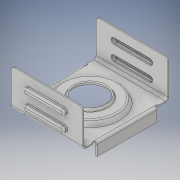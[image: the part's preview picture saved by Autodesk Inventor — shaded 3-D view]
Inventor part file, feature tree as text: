
AUTODESK INVENTOR PART (.ipt)
format: ipt  version: 2019 (Build 230136000, 136)  size: 508,928 bytes
history: native  units: mm
features: sketch x9, sheet_metal_op x5, plane x4, fillet x3, chamfer x2, shell x2, revolve x1, extrude x1, mirror x1, other x1
ambient origin geometry x8: Origin, YZ Plane, XZ Plane, XY Plane, X Axis, Y Axis, Z Axis, Center Point
bodies: Solid1 (feature_tree)
feature tree (29):
  sheet_metal_op  "Face1"
  sheet_metal_op  "Fold1"
  sheet_metal_op  "Fold2"
  sheet_metal_op  "Fold3"
  sheet_metal_op  "Fold4"
  plane  "Work Plane2"
  revolve  "Revolution1"  [1 undecoded]
  fillet  "Fillet1"  Radius=6.5mm
  chamfer  "Chamfer2"  Distance=3.0mm
  chamfer  "Corner Round1"
  plane  "Work Plane3"
  sketch  "Sketch9"  dims[d17=0.1mm]
  sketch  "Sketch10"  dims[d18=90.0deg d19=0.1mm]
  sketch  "Sketch11"  dims[d20=0.1mm d21=0.05mm d22=0.2mm d23=0.1mm d24=90.0deg d25=0.1mm d26=3.0mm d27=0.1mm d28=0.05mm d29=0.2mm d30=0.1mm d31=90.0deg d32=0.2mm d33=3.0mm d34=0.1mm d35=0.05mm d36=0.2mm d37=0.1mm d38=90.0deg d39=0.2mm d42=-3.087mm d43=0.5mm d44=120.0deg d45=0.75mm d46=120.0deg d47=0.25mm d48=120.0deg d50=120.0deg d52=0.1mm d53=0.1mm d54=0.1mm d55=2.5mm d56=90.0deg d57=0.15mm d58=0.05mm d62=0.115mm d63=0.08mm d64=45.0deg d65=0.3mm d66=3.0mm d67=3.0mm d68=0.75mm d69=0.75mm d70=0.5mm d71=0.5mm d72=0.25mm d73=-1.25mm d74=3.0mm d77=0.2mm d78=0.4mm d81=0.15mm d82=0.15mm d83=0.3mm d84=0.0mm d85=0.15mm d86=0.1mm d88=-3.6085mm d89=-0.875mm d90=0.1mm d91=0.0999mm]
  extrude  "Extrusion2"  Depth=4.0mm
  fillet  "Fillet2"  Radius=1.5mm
  shell  "Shell1"  Thickness=0.25mm
  plane  "Work Plane5"
  plane  "Work Plane6"
  mirror  "Mirror1"
  shell  "Shell2"  Thickness=0.25mm
  fillet  "Fillet4"  Radius=0.1mm
  sketch  "Sketch1"  dims[d0=13.0mm d1=6.0mm d2=6.5mm d3=3.0mm d4=5.0mm]
  other  "Plate1"
  sketch  "Sketch2"  dims[d7=5.0mm d8=4.0mm d9=1.5mm d10=0.25mm d11=0.25mm d12=0.1mm]
  sketch  "Sketch3"  dims[d13=1.0mm]
  sketch  "Sketch4"  dims[d14=0.1mm]
  sketch  "Sketch5"  dims[d15=0.05mm]
  sketch  "Sketch8"  dims[d16=0.2mm]
note: 1 required parameter value undecoded (feature->parameter linkage not recoverable at this tier; creation-order binding heuristic only, values carry confidence <= 0.55)
